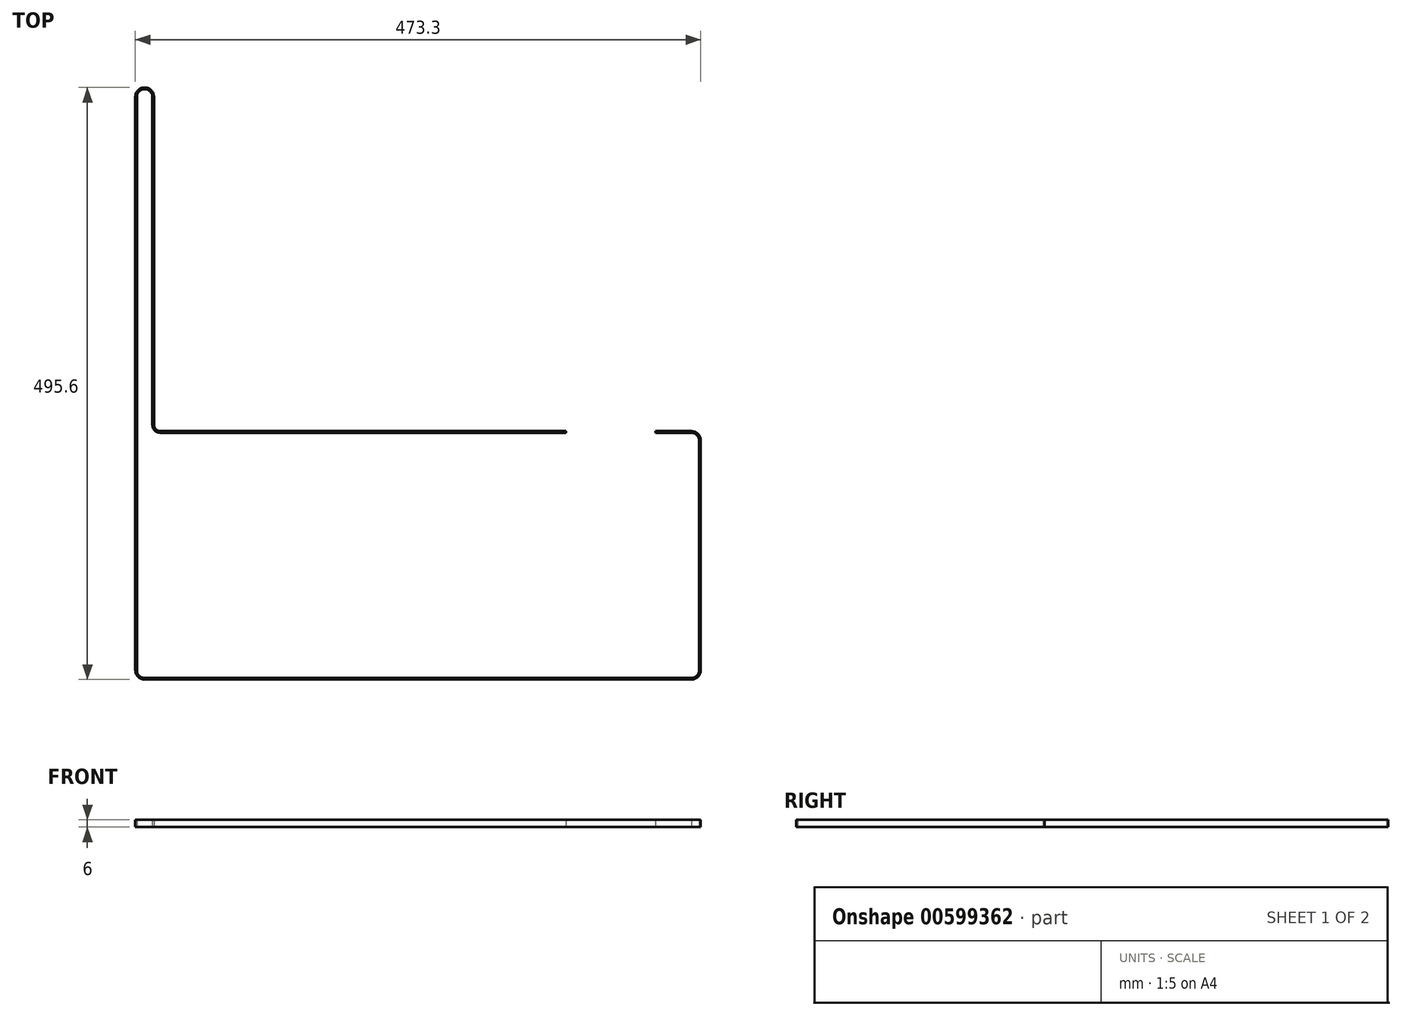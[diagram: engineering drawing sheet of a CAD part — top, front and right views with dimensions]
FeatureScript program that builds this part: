
annotation { "Feature Type Name" : "Feature", "Feature Type Description" : "" }
export const myFeature = defineFeature(function(context is Context, id is Id, definition is map)
    precondition{}
    {
        {
            var Q0;
            Q0=qCreatedBy(makeId("Top.planeOp"),FACE);
            var sketch = newSketch(context, id + "F0", { "sketchPlane" : qUnion([Q0])});
            skArc(sketch, "E0", {"start": v(-188.46, 326.6) * mm, "mid": v(-194.96, 333.1) * mm, "end": v(-201.46, 326.6) * mm});
            skArc(sketch, "E1", {"start": v(-201.46, -153.4) * mm, "mid": v(-199.56, -158) * mm, "end": v(-194.96, -159.9) * mm});
            skArc(sketch, "E2", {"start": v(262.74, -159.9) * mm, "mid": v(267.33, -158) * mm, "end": v(269.24, -153.4) * mm});
            skCircle(sketch, "E3", {"center": v(-194.96, 326.6) * mm, "radius": 2.55 * mm, "construction": true});
            skLineSegment(sketch, "E4", {"start": v(262.74, -159.9) * mm, "end": v(-194.96, -159.9) * mm});
            skLineSegment(sketch, "E5", {"start": v(-201.46, -153.4) * mm, "end": v(-201.46, 326.6) * mm});
            skLineSegment(sketch, "E6", {"start": v(-188.46, 326.6) * mm, "end": v(-188.46, 51.95) * mm});
            skArc(sketch, "E7", {"start": v(-188.46, 51.95) * mm, "mid": v(-186.56, 47.36) * mm, "end": v(-181.96, 45.45) * mm});
            skArc(sketch, "E8", {"start": v(269.24, 38.95) * mm, "mid": v(267.38, 43.5) * mm, "end": v(262.88, 45.45) * mm});
            skLineSegment(sketch, "E9", {"start": v(269.24, -153.4) * mm, "end": v(269.24, 38.95) * mm});
            skArc(sketch, "E10.0", {"start": v(-187.16, 51.95) * mm, "mid": v(-185.64, 48.28) * mm, "end": v(-181.96, 46.75) * mm});
            skArc(sketch, "E11.0", {"start": v(270.54, 38.95) * mm, "mid": v(268.26, 44.46) * mm, "end": v(262.77, 46.75) * mm});
            skArc(sketch, "E12.0", {"start": v(262.74, -161.2) * mm, "mid": v(268.25, -158.91) * mm, "end": v(270.54, -153.4) * mm});
            skArc(sketch, "E13.0", {"start": v(-202.76, -153.4) * mm, "mid": v(-200.48, -158.91) * mm, "end": v(-194.96, -161.2) * mm});
            skLineSegment(sketch, "E14", {"start": v(-202.76, 326.6) * mm, "end": v(-202.76, -153.4) * mm});
            skLineSegment(sketch, "E15", {"start": v(-194.96, -161.2) * mm, "end": v(262.74, -161.2) * mm});
            skLineSegment(sketch, "E16", {"start": v(270.54, -153.4) * mm, "end": v(270.54, 38.95) * mm});
            skLineSegment(sketch, "E17", {"start": v(-187.16, 51.95) * mm, "end": v(-187.16, 326.6) * mm});
            skLineSegment(sketch, "E18", {"start": v(-181.96, 46.75) * mm, "end": v(157.74, 46.75) * mm});
            skLineSegment(sketch, "E19", {"start": v(262.88, 45.45) * mm, "end": v(232.74, 45.45) * mm});
            skArc(sketch, "E20.trimOffspring", {"start": v(-187.16, 326.6) * mm, "mid": v(-194.96, 334.4) * mm, "end": v(-202.76, 326.6) * mm});
            skLineSegment(sketch, "E21", {"start": v(232.74, 46.75) * mm, "end": v(232.74, 45.45) * mm});
            skLineSegment(sketch, "E22", {"start": v(157.74, 46.75) * mm, "end": v(157.74, 45.45) * mm});
            skLineSegment(sketch, "E23.trimOffspring", {"start": v(232.74, 46.75) * mm, "end": v(262.77, 46.75) * mm});
            skLineSegment(sketch, "E24.trimOffspring", {"start": v(157.74, 45.45) * mm, "end": v(-181.96, 45.45) * mm});
            skSolve(sketch);
        }
        {
            var Q0;
            Q0=qSketchRegion(id+"F0",true);
            extrude(context, id + "F1", {"entities" : qUnion([Q0]), "depth" : 6 * mm});
        }
    });
